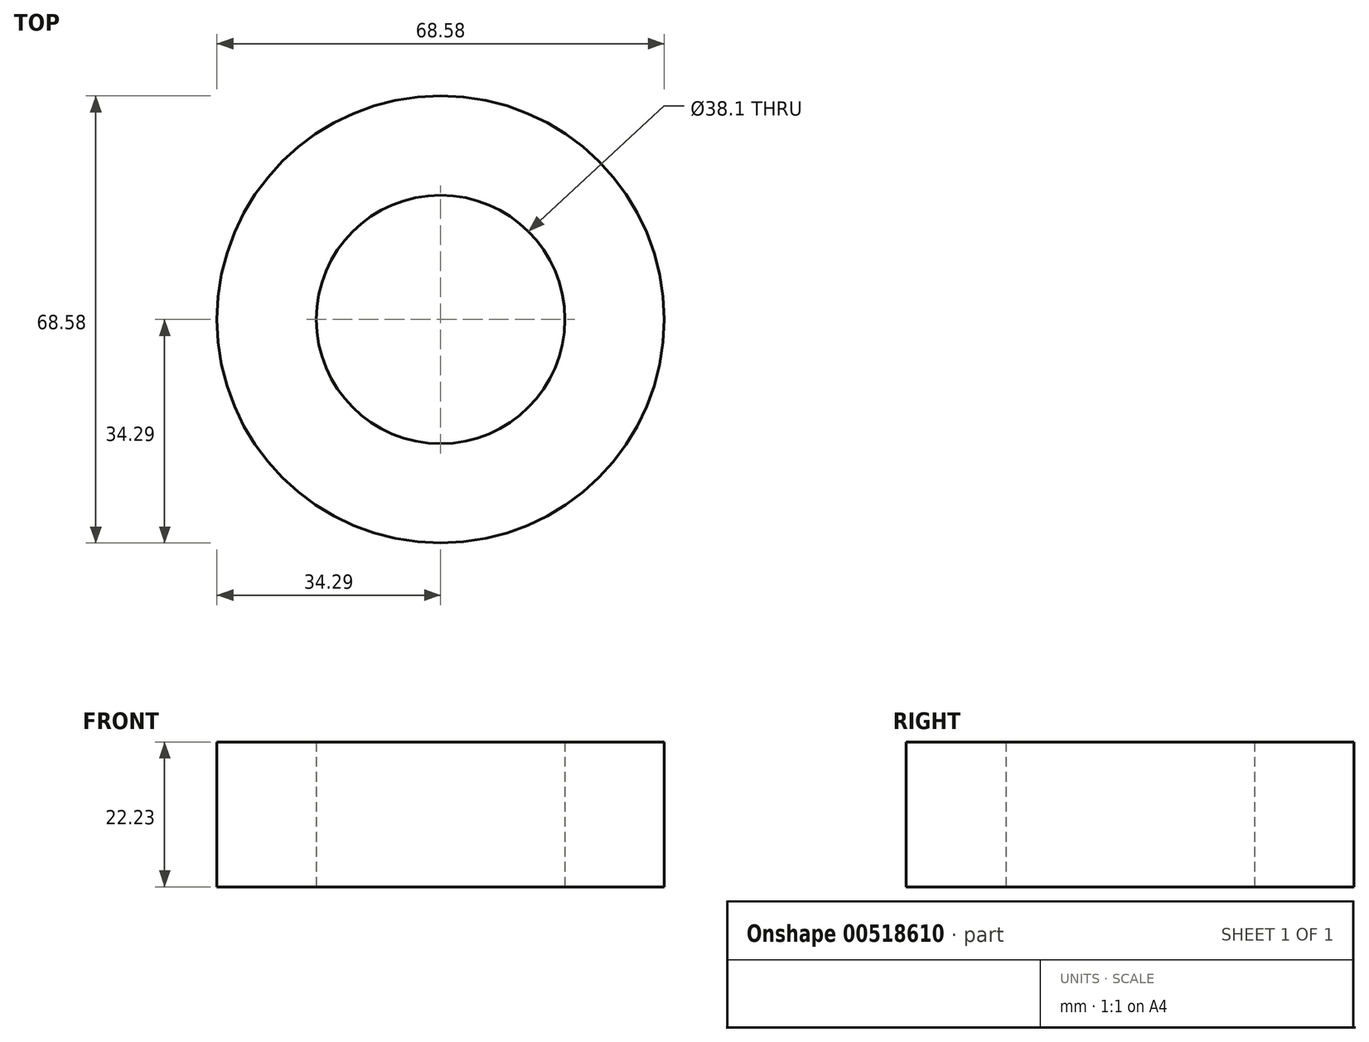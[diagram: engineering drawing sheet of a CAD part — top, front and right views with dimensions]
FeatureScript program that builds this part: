
annotation { "Feature Type Name" : "Feature", "Feature Type Description" : "" }
export const myFeature = defineFeature(function(context is Context, id is Id, definition is map)
    precondition{}
    {
        {
            var Q0;
            Q0=qCreatedBy(makeId("Top.planeOp"),FACE);
            var sketch = newSketch(context, id + "F0", { "sketchPlane" : qUnion([Q0])});
            skCircle(sketch, "E0", {"center": v(0, 0) * mm, "radius": 34.3 * mm});
            skCircle(sketch, "E1", {"center": v(0, 0) * mm, "radius": 19.05 * mm});
            skSolve(sketch);
        }
        {
            var Q0;
            Q0=makeQuery(id+"F0.imprint","IMPRINT",FACE,{"disambiguationData":[TD([[makeQuery(id+"F0.imprint","IMPRINT",EDGE,{"derivedFrom":sQuery(id+"F0.wireOp",EDGE,"E0")}),1.0]])]});
            extrude(context, id + "F1", {"entities" : qUnion([Q0]), "depth" : 22.22 * mm, "offsetDistance" : 25.4 * mm});
        }
    });
